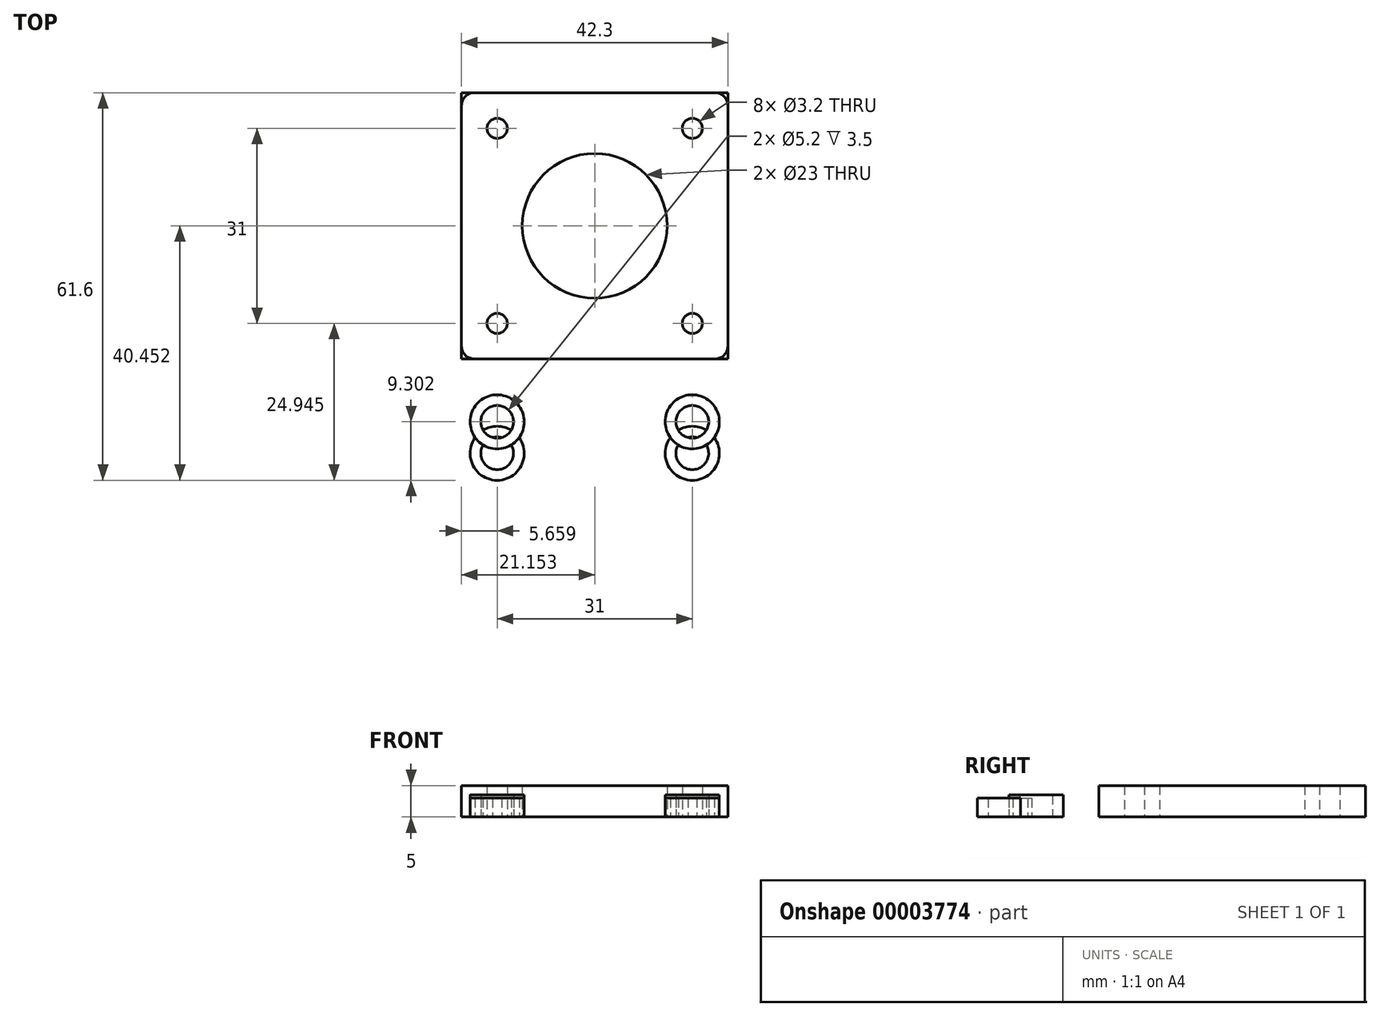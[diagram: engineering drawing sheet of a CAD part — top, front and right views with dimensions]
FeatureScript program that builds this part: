
annotation { "Feature Type Name" : "Feature", "Feature Type Description" : "" }
export const myFeature = defineFeature(function(context is Context, id is Id, definition is map)
    precondition{}
    {
        {
            var Q0;
            Q0=qCreatedBy(makeId("Top.planeOp"),FACE);
            var sketch = newSketch(context, id + "F0", { "sketchPlane" : qUnion([Q0])});
            skLineSegment(sketch, "E0.bottom", {"start": v(-21.16, 21.21) * mm, "end": v(21.14, 21.21) * mm});
            skLineSegment(sketch, "E0.top", {"start": v(-21.16, -21.09) * mm, "end": v(21.14, -21.09) * mm});
            skLineSegment(sketch, "E0.left", {"start": v(-21.16, 21.21) * mm, "end": v(-21.16, -21.09) * mm});
            skLineSegment(sketch, "E0.right", {"start": v(21.14, 21.21) * mm, "end": v(21.14, -21.09) * mm});
            skLineSegment(sketch, "E1", {"start": v(-21.16, 21.21) * mm, "end": v(21.14, -21.09) * mm, "construction": true});
            skLineSegment(sketch, "E2", {"start": v(21.14, 21.21) * mm, "end": v(-21.16, -21.09) * mm, "construction": true});
            skCircle(sketch, "E3", {"center": v(0, 0.06) * mm, "radius": 11.5 * mm});
            skCircle(sketch, "E4", {"center": v(-15.5, 15.55) * mm, "radius": 1.6 * mm});
            skCircle(sketch, "E5.0.1.0", {"center": v(-15.5, -15.45) * mm, "radius": 1.6 * mm});
            skCircle(sketch, "E5.1.0.0", {"center": v(15.5, 15.55) * mm, "radius": 1.6 * mm});
            skCircle(sketch, "E5.1.1.0", {"center": v(15.5, -15.45) * mm, "radius": 1.6 * mm});
            skLineSegment(sketch, "E5.direction1", {"start": v(-15.5, 15.55) * mm, "end": v(15.5, 15.55) * mm, "construction": true});
            skLineSegment(sketch, "E5.direction2", {"start": v(-15.5, 15.55) * mm, "end": v(-15.5, -15.45) * mm, "construction": true});
            skLineSegment(sketch, "E6.top", {"start": v(-21.16, -41.09) * mm, "end": v(21.14, -41.09) * mm});
            skLineSegment(sketch, "E6.left", {"start": v(-21.16, -21.09) * mm, "end": v(-21.16, -41.09) * mm});
            skLineSegment(sketch, "E6.right", {"start": v(21.14, -21.09) * mm, "end": v(21.14, -41.09) * mm});
            skLineSegment(sketch, "E7", {"start": v(-21.16, -31.09) * mm, "end": v(21.14, -31.09) * mm, "construction": true});
            skLineSegment(sketch, "E8", {"start": v(-15.5, -15.45) * mm, "end": v(-15.5, -31.09) * mm, "construction": true});
            skLineSegment(sketch, "E9", {"start": v(15.5, -15.45) * mm, "end": v(15.5, -31.09) * mm, "construction": true});
            skCircle(sketch, "E10", {"center": v(-15.5, -31.09) * mm, "radius": 2.6 * mm});
            skCircle(sketch, "E11", {"center": v(15.5, -31.09) * mm, "radius": 2.6 * mm});
            skCircle(sketch, "E12", {"center": v(-15.5, -31.09) * mm, "radius": 4.3 * mm});
            skCircle(sketch, "E13", {"center": v(15.5, -31.09) * mm, "radius": 4.3 * mm});
            skSolve(sketch);
        }
        {
            var Q0;
            Q0=makeQuery(id+"F0.imprint","IMPRINT",FACE,{"disambiguationData":[TD([[makeQuery(id+"F0.imprint","IMPRINT",EDGE,{"derivedFrom":sQuery(id+"F0.wireOp",EDGE,"E0.bottom")}),-1.0]])]});
            var Q1;
            Q1=makeQuery(id+"F0.imprint","IMPRINT",FACE,{"disambiguationData":[TD([[makeQuery(id+"F0.imprint","IMPRINT",EDGE,{"derivedFrom":sQuery(id+"F0.wireOp",EDGE,"E0.top")}),-1.0]])]});
            extrude(context, id + "F1", {"entities" : qUnion([Q0, Q1]), "depth" : 5 * mm});
        }
        {
            var Q0;
            Q0=makeQuery(id+"F1.opExtrude","SWEPT_EDGE",EDGE,{"disambiguationData":[OSD([sQuery(id+"F0.wireOp",EDGE,"E6.top"),sQuery(id+"F0.wireOp",EDGE,"E6.left")])]});
            var Q1;
            Q1=makeQuery(id+"F1.opExtrude","SWEPT_EDGE",EDGE,{"disambiguationData":[OSD([sQuery(id+"F0.wireOp",EDGE,"E6.top"),sQuery(id+"F0.wireOp",EDGE,"E6.right")])]});
            var Q2;
            Q2=makeQuery(id+"F1.opExtrude","SWEPT_EDGE",EDGE,{"disambiguationData":[OSD([sQuery(id+"F0.wireOp",EDGE,"E0.bottom"),sQuery(id+"F0.wireOp",EDGE,"E0.right")])]});
            var Q3;
            Q3=makeQuery(id+"F1.opExtrude","SWEPT_EDGE",EDGE,{"disambiguationData":[OSD([sQuery(id+"F0.wireOp",EDGE,"E0.bottom"),sQuery(id+"F0.wireOp",EDGE,"E0.left")])]});
            fillet(context, id + "F2", {"entities" : qUnion([Q0, Q1, Q2, Q3]), "radius" : 2 * mm, "tangentPropagation" : true, "allowEdgeOverflow" : false});
        }
        {
            var Q0;
            Q0=makeQuery(id+"F0.imprint","IMPRINT",FACE,{"disambiguationData":[TD([[makeQuery(id+"F0.imprint","IMPRINT",EDGE,{"derivedFrom":sQuery(id+"F0.wireOp",EDGE,"E10")}),-1.0]])]});
            extrude(context, id + "F3", {"entities" : qUnion([Q0]), "operationType" : NewBodyOperationType.ADD, "depth" : 3.5 * mm});
        }
        {
            var Q0;
            Q0=makeQuery(id+"F0.imprint","IMPRINT",FACE,{"disambiguationData":[TD([[makeQuery(id+"F0.imprint","IMPRINT",EDGE,{"derivedFrom":sQuery(id+"F0.wireOp",EDGE,"E11")}),-1.0]])]});
            extrude(context, id + "F4", {"entities" : qUnion([Q0]), "operationType" : NewBodyOperationType.ADD, "depth" : 3.5 * mm});
        }
        {
            var Q0;
            Q0=qCreatedBy(makeId("Top.planeOp"),FACE);
            var sketch = newSketch(context, id + "F5", { "sketchPlane" : qUnion([Q0])});
            skLineSegment(sketch, "E14.bottom", {"start": v(-21.16, 21.21) * mm, "end": v(21.14, 21.21) * mm});
            skLineSegment(sketch, "E14.top", {"start": v(-21.16, -21.09) * mm, "end": v(21.14, -21.09) * mm});
            skLineSegment(sketch, "E14.left", {"start": v(-21.16, 21.21) * mm, "end": v(-21.16, -21.09) * mm});
            skLineSegment(sketch, "E14.right", {"start": v(21.14, 21.21) * mm, "end": v(21.14, -21.09) * mm});
            skLineSegment(sketch, "E15", {"start": v(-21.16, 21.21) * mm, "end": v(21.14, -21.09) * mm, "construction": true});
            skLineSegment(sketch, "E16", {"start": v(21.14, 21.21) * mm, "end": v(-21.16, -21.09) * mm, "construction": true});
            skCircle(sketch, "E17", {"center": v(0, 0.06) * mm, "radius": 11.5 * mm});
            skCircle(sketch, "E18", {"center": v(-15.5, 15.55) * mm, "radius": 1.6 * mm});
            skCircle(sketch, "E19.0.1.0", {"center": v(-15.5, -15.45) * mm, "radius": 1.6 * mm});
            skCircle(sketch, "E19.1.0.0", {"center": v(15.5, 15.55) * mm, "radius": 1.6 * mm});
            skCircle(sketch, "E19.1.1.0", {"center": v(15.5, -15.45) * mm, "radius": 1.6 * mm});
            skLineSegment(sketch, "E19.direction1", {"start": v(-15.5, 15.55) * mm, "end": v(15.5, 15.55) * mm, "construction": true});
            skLineSegment(sketch, "E19.direction2", {"start": v(-15.5, 15.55) * mm, "end": v(-15.5, -15.45) * mm, "construction": true});
            skLineSegment(sketch, "E20.top", {"start": v(-21.16, -51.09) * mm, "end": v(21.14, -51.09) * mm});
            skLineSegment(sketch, "E20.left", {"start": v(-21.16, -21.09) * mm, "end": v(-21.16, -51.09) * mm});
            skLineSegment(sketch, "E20.right", {"start": v(21.14, -21.09) * mm, "end": v(21.14, -51.09) * mm});
            skLineSegment(sketch, "E21", {"start": v(-21.16, -36.09) * mm, "end": v(21.14, -36.09) * mm, "construction": true});
            skLineSegment(sketch, "E22", {"start": v(-15.5, -15.45) * mm, "end": v(-15.5, -36.09) * mm, "construction": true});
            skLineSegment(sketch, "E23", {"start": v(15.5, -15.45) * mm, "end": v(15.5, -36.09) * mm, "construction": true});
            skCircle(sketch, "E24", {"center": v(-15.5, -36.09) * mm, "radius": 2.6 * mm});
            skCircle(sketch, "E25", {"center": v(15.5, -36.09) * mm, "radius": 2.6 * mm});
            skCircle(sketch, "E26", {"center": v(-15.5, -36.09) * mm, "radius": 4.3 * mm});
            skCircle(sketch, "E27", {"center": v(15.5, -36.09) * mm, "radius": 4.3 * mm});
            skSolve(sketch);
        }
        {
            var Q0;
            Q0=makeQuery(id+"F5.imprint","IMPRINT",FACE,{"disambiguationData":[TD([[makeQuery(id+"F5.imprint","IMPRINT",EDGE,{"derivedFrom":sQuery(id+"F5.wireOp",EDGE,"E14.bottom")}),-1.0]])]});
            var Q1;
            Q1=makeQuery(id+"F5.imprint","IMPRINT",FACE,{"disambiguationData":[TD([[makeQuery(id+"F5.imprint","IMPRINT",EDGE,{"derivedFrom":sQuery(id+"F5.wireOp",EDGE,"E14.top")}),-1.0]])]});
            extrude(context, id + "F6", {"entities" : qUnion([Q0, Q1]), "depth" : 5 * mm});
        }
        {
            var Q0;
            Q0=makeQuery(id+"F5.imprint","IMPRINT",FACE,{"disambiguationData":[TD([[makeQuery(id+"F5.imprint","IMPRINT",EDGE,{"derivedFrom":sQuery(id+"F5.wireOp",EDGE,"E24")}),-1.0]])]});
            var Q1;
            Q1=makeQuery(id+"F5.imprint","IMPRINT",FACE,{"disambiguationData":[TD([[makeQuery(id+"F5.imprint","IMPRINT",EDGE,{"derivedFrom":sQuery(id+"F5.wireOp",EDGE,"E25")}),-1.0]])]});
            extrude(context, id + "F7", {"entities" : qUnion([Q0, Q1]), "operationType" : NewBodyOperationType.ADD, "depth" : 3 * mm});
        }
    });
